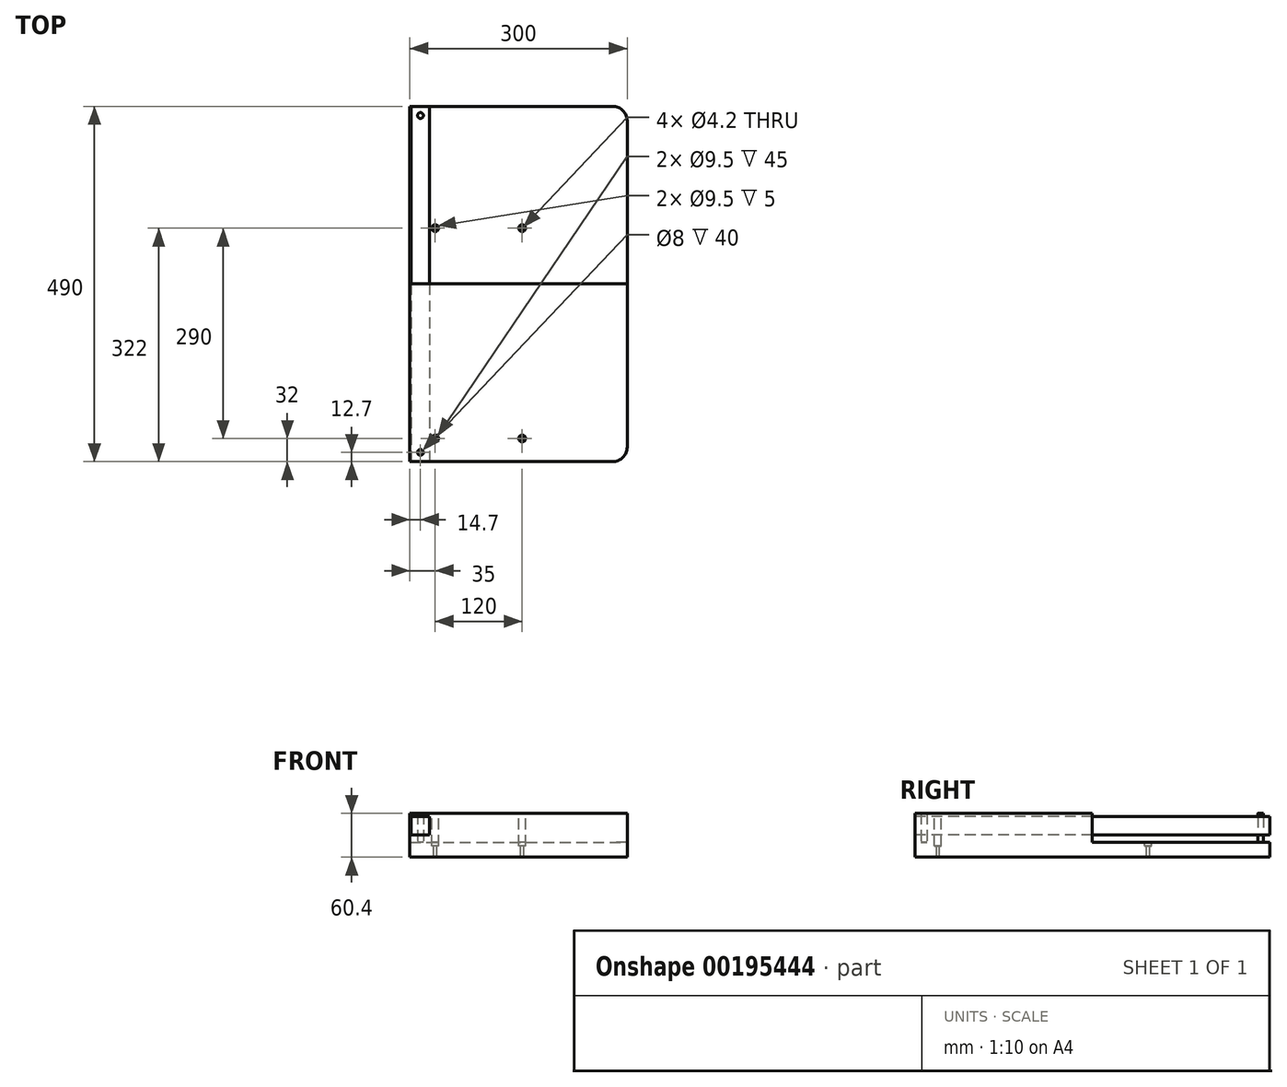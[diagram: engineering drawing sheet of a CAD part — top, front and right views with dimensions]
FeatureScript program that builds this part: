
annotation { "Feature Type Name" : "Feature", "Feature Type Description" : "" }
export const myFeature = defineFeature(function(context is Context, id is Id, definition is map)
    precondition{}
    {
        {
            var Q0;
            Q0=qCreatedBy(makeId("Top.planeOp"),FACE);
            var sketch = newSketch(context, id + "F0", { "sketchPlane" : qUnion([Q0])});
            skLineSegment(sketch, "E0.bottom", {"start": v(0, 0) * mm, "end": v(300, 0) * mm});
            skLineSegment(sketch, "E0.top", {"start": v(0, 490) * mm, "end": v(300, 490) * mm});
            skLineSegment(sketch, "E0.left", {"start": v(0, 0) * mm, "end": v(0, 490) * mm});
            skLineSegment(sketch, "E0.right", {"start": v(300, 0) * mm, "end": v(300, 490) * mm});
            skSolve(sketch);
        }
        {
            var Q0;
            Q0=makeQuery(id+"F0.imprint","IMPRINT",FACE,{"disambiguationData":[TD([[makeQuery(id+"F0.imprint","IMPRINT",EDGE,{"derivedFrom":sQuery(id+"F0.wireOp",EDGE,"E0.bottom")}),1.0]])]});
            extrude(context, id + "F1", {"entities" : qUnion([Q0]), "depth" : 20.4 * mm});
        }
        {
            var Q0;
            Q0=makeQuery(id+"F1.opExtrude","CAP_FACE",FACE,{"disambiguationData":[OSD([sQuery(id+"F0.wireOp",EDGE,"E0.bottom"),sQuery(id+"F0.wireOp",EDGE,"E0.top"),sQuery(id+"F0.wireOp",EDGE,"E0.left"),sQuery(id+"F0.wireOp",EDGE,"E0.right")])],"isStart":false});
            var sketch = newSketch(context, id + "F2", { "sketchPlane" : qUnion([Q0])});
            skCircle(sketch, "E1", {"center": v(35, 32) * mm, "radius": 4.75 * mm});
            skCircle(sketch, "E2", {"center": v(35, 32) * mm, "radius": 2.1 * mm});
            skCircle(sketch, "E3.0.1.0", {"center": v(35, 322) * mm, "radius": 4.75 * mm});
            skCircle(sketch, "E3.0.1.1", {"center": v(35, 322) * mm, "radius": 2.1 * mm});
            skCircle(sketch, "E3.1.0.0", {"center": v(155, 32) * mm, "radius": 4.75 * mm});
            skCircle(sketch, "E3.1.0.1", {"center": v(155, 32) * mm, "radius": 2.1 * mm});
            skCircle(sketch, "E3.1.1.0", {"center": v(155, 322) * mm, "radius": 4.75 * mm});
            skCircle(sketch, "E3.1.1.1", {"center": v(155, 322) * mm, "radius": 2.1 * mm});
            skLineSegment(sketch, "E3.direction1", {"start": v(35, 32) * mm, "end": v(155, 32) * mm, "construction": true});
            skLineSegment(sketch, "E3.direction2", {"start": v(35, 32) * mm, "end": v(35, 322) * mm, "construction": true});
            skSolve(sketch);
        }
        {
            var Q0;
            Q0=makeQuery(id+"F2.imprint","IMPRINT",FACE,{"disambiguationData":[TD([[makeQuery(id+"F2.imprint","IMPRINT",EDGE,{"derivedFrom":sQuery(id+"F2.wireOp",EDGE,"E1")}),1.0]])]});
            var Q1;
            Q1=makeQuery(id+"F2.imprint","IMPRINT",FACE,{"disambiguationData":[TD([[makeQuery(id+"F2.imprint","IMPRINT",EDGE,{"derivedFrom":sQuery(id+"F2.wireOp",EDGE,"E3.1.0.0")}),1.0]])]});
            var Q2;
            Q2=makeQuery(id+"F2.imprint","IMPRINT",FACE,{"disambiguationData":[TD([[makeQuery(id+"F2.imprint","IMPRINT",EDGE,{"derivedFrom":sQuery(id+"F2.wireOp",EDGE,"E3.0.1.0")}),1.0]])]});
            var Q3;
            Q3=makeQuery(id+"F2.imprint","IMPRINT",FACE,{"disambiguationData":[TD([[makeQuery(id+"F2.imprint","IMPRINT",EDGE,{"derivedFrom":sQuery(id+"F2.wireOp",EDGE,"E3.1.1.0")}),1.0]])]});
            extrude(context, id + "F3", {"entities" : qUnion([Q0, Q1, Q2, Q3]), "operationType" : NewBodyOperationType.REMOVE, "oppositeDirection" : true, "depth" : 5 * mm});
        }
        {
            var Q0;
            Q0=makeQuery(id+"F3.boolean.opBoolean","SPLIT",FACE,{"disambiguationData":[TD([makeQuery(id+"F3.opExtrude","SWEPT_FACE",FACE,{"disambiguationData":[OSD([sQuery(id+"F2.wireOp",EDGE,"E2")])]})])],"derivedFrom":makeQuery(id+"F1.opExtrude","CAP_FACE",FACE,{"disambiguationData":[OSD([sQuery(id+"F0.wireOp",EDGE,"E0.bottom"),sQuery(id+"F0.wireOp",EDGE,"E0.top"),sQuery(id+"F0.wireOp",EDGE,"E0.left"),sQuery(id+"F0.wireOp",EDGE,"E0.right")])],"isStart":false})});
            var Q1;
            Q1=makeQuery(id+"F3.boolean.opBoolean","SPLIT",FACE,{"disambiguationData":[TD([makeQuery(id+"F3.opExtrude","SWEPT_FACE",FACE,{"disambiguationData":[OSD([sQuery(id+"F2.wireOp",EDGE,"E3.1.0.1")])]})])],"derivedFrom":makeQuery(id+"F1.opExtrude","CAP_FACE",FACE,{"disambiguationData":[OSD([sQuery(id+"F0.wireOp",EDGE,"E0.bottom"),sQuery(id+"F0.wireOp",EDGE,"E0.top"),sQuery(id+"F0.wireOp",EDGE,"E0.left"),sQuery(id+"F0.wireOp",EDGE,"E0.right")])],"isStart":false})});
            var Q2;
            Q2=makeQuery(id+"F3.boolean.opBoolean","SPLIT",FACE,{"disambiguationData":[TD([makeQuery(id+"F3.opExtrude","SWEPT_FACE",FACE,{"disambiguationData":[OSD([sQuery(id+"F2.wireOp",EDGE,"E3.0.1.1")])]})])],"derivedFrom":makeQuery(id+"F1.opExtrude","CAP_FACE",FACE,{"disambiguationData":[OSD([sQuery(id+"F0.wireOp",EDGE,"E0.bottom"),sQuery(id+"F0.wireOp",EDGE,"E0.top"),sQuery(id+"F0.wireOp",EDGE,"E0.left"),sQuery(id+"F0.wireOp",EDGE,"E0.right")])],"isStart":false})});
            var Q3;
            Q3=makeQuery(id+"F3.boolean.opBoolean","SPLIT",FACE,{"disambiguationData":[TD([makeQuery(id+"F3.opExtrude","SWEPT_FACE",FACE,{"disambiguationData":[OSD([sQuery(id+"F2.wireOp",EDGE,"E3.1.1.1")])]})])],"derivedFrom":makeQuery(id+"F1.opExtrude","CAP_FACE",FACE,{"disambiguationData":[OSD([sQuery(id+"F0.wireOp",EDGE,"E0.bottom"),sQuery(id+"F0.wireOp",EDGE,"E0.top"),sQuery(id+"F0.wireOp",EDGE,"E0.left"),sQuery(id+"F0.wireOp",EDGE,"E0.right")])],"isStart":false})});
            extrude(context, id + "F4", {"entities" : qUnion([Q0, Q1, Q2, Q3]), "operationType" : NewBodyOperationType.REMOVE, "oppositeDirection" : true, "depth" : 25 * mm});
        }
        {
            var Q0;
            Q0=makeQuery(id+"F1.opExtrude","SWEPT_EDGE",EDGE,{"disambiguationData":[OSD([sQuery(id+"F0.wireOp",EDGE,"E0.bottom"),sQuery(id+"F0.wireOp",EDGE,"E0.right")])]});
            var Q1;
            Q1=makeQuery(id+"F1.opExtrude","SWEPT_EDGE",EDGE,{"disambiguationData":[OSD([sQuery(id+"F0.wireOp",EDGE,"E0.top"),sQuery(id+"F0.wireOp",EDGE,"E0.right")])]});
            fillet(context, id + "F5", {"entities" : qUnion([Q0, Q1]), "radius" : 20 * mm, "tangentPropagation" : true, "allowEdgeOverflow" : false});
        }
        {
            var Q0;
            {var subQ0=sQuery(id+"F0.wireOp",EDGE,"E0.left");var subQ1=sQuery(id+"F0.wireOp",EDGE,"E0.top");var subQ2=sQuery(id+"F0.wireOp",EDGE,"E0.right");var subQ3=sQuery(id+"F0.wireOp",EDGE,"E0.bottom");Q0=makeQuery(id+"F3.boolean.opBoolean","SPLIT",FACE,{"disambiguationData":[TD([makeQuery(id+"F1.opExtrude","SWEPT_FACE",FACE,{"disambiguationData":[OSD([subQ3])]})])],"derivedFrom":makeQuery(id+"F1.opExtrude","CAP_FACE",FACE,{"disambiguationData":[OSD([subQ3,subQ1,subQ0,subQ2])],"isStart":false})});}
            var sketch = newSketch(context, id + "F6", { "sketchPlane" : qUnion([Q0])});
            skCircle(sketch, "E4", {"center": v(14.7, 477.3) * mm, "radius": 4 * mm});
            skLineSegment(sketch, "E5", {"start": v(0, 245) * mm, "end": v(300, 245) * mm});
            skCircle(sketch, "E6.MirrorC", {"center": v(14.7, 12.7) * mm, "radius": 4 * mm});
            skSolve(sketch);
        }
        {
            var Q0;
            Q0=makeQuery(id+"F6.imprint","IMPRINT",FACE,{"disambiguationData":[TD([[makeQuery(id+"F6.imprint","IMPRINT",EDGE,{"derivedFrom":sQuery(id+"F6.wireOp",EDGE,"E6.MirrorC")}),-1.0]])]});
            var Q1;
            Q1=makeQuery(id+"F6.imprint","IMPRINT",FACE,{"disambiguationData":[TD([[makeQuery(id+"F6.imprint","IMPRINT",EDGE,{"derivedFrom":sQuery(id+"F6.wireOp",EDGE,"E4")}),1.0]])]});
            extrude(context, id + "F7", {"entities" : qUnion([Q0, Q1]), "operationType" : NewBodyOperationType.ADD, "depth" : 40 * mm});
        }
        {
            var Q0;
            Q0=makeQuery(id+"F1.opExtrude","SWEPT_FACE",FACE,{"disambiguationData":[OSD([sQuery(id+"F0.wireOp",EDGE,"E0.bottom")])]});
            var sketch = newSketch(context, id + "F8", { "sketchPlane" : qUnion([Q0])});
            skLineSegment(sketch, "E7.bottom", {"start": v(27.4, 30.4) * mm, "end": v(2, 30.4) * mm});
            skLineSegment(sketch, "E7.top", {"start": v(27.4, 55.8) * mm, "end": v(2, 55.8) * mm});
            skLineSegment(sketch, "E7.left", {"start": v(27.4, 30.4) * mm, "end": v(27.4, 55.8) * mm});
            skLineSegment(sketch, "E7.right", {"start": v(2, 30.4) * mm, "end": v(2, 55.8) * mm});
            skPoint(sketch, "E7.middle", {"position": v(14.7, 43.1) * mm});
            skSolve(sketch);
        }
        {
            var Q0;
            Q0=makeQuery(id+"F8.imprint","IMPRINT",FACE,{"disambiguationData":[TD([[makeQuery(id+"F8.imprint","IMPRINT",EDGE,{"derivedFrom":sQuery(id+"F8.wireOp",EDGE,"E7.bottom")}),-1.0]])]});
            var Q1;
            Q1=makeQuery(id+"F1.opExtrude","SWEPT_FACE",FACE,{"disambiguationData":[OSD([sQuery(id+"F0.wireOp",EDGE,"E0.top")])]});
            extrude(context, id + "F9", {"entities" : qUnion([Q0]), "endBound" : BoundingType.UP_TO_SURFACE, "oppositeDirection" : true, "endBoundEntityFace" : qUnion([Q1]), "depth" : 25 * mm});
        }
    });
